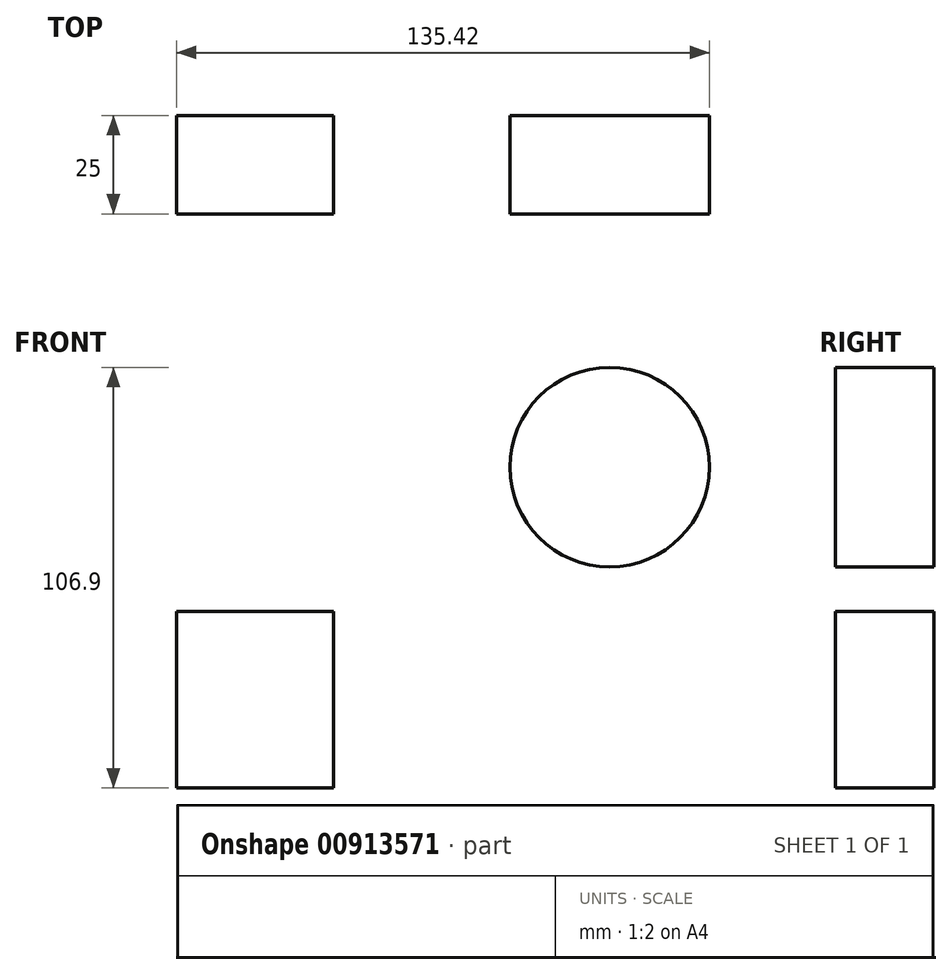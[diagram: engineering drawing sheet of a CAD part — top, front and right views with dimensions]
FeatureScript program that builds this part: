
annotation { "Feature Type Name" : "Feature", "Feature Type Description" : "" }
export const myFeature = defineFeature(function(context is Context, id is Id, definition is map)
    precondition{}
    {
        {
            var Q0;
            Q0=qCreatedBy(makeId("Front.planeOp"),FACE);
            var sketch = newSketch(context, id + "F0", { "sketchPlane" : qUnion([Q0])});
            skLineSegment(sketch, "E0.bottom", {"start": v(-147.56, 0) * mm, "end": v(-107.64, 0) * mm});
            skLineSegment(sketch, "E0.top", {"start": v(-147.56, -44.9) * mm, "end": v(-107.64, -44.9) * mm});
            skLineSegment(sketch, "E0.left", {"start": v(-147.56, 0) * mm, "end": v(-147.56, -44.9) * mm});
            skLineSegment(sketch, "E0.right", {"start": v(-107.64, 0) * mm, "end": v(-107.64, -44.9) * mm});
            skCircle(sketch, "E1", {"center": v(-37.5, 36.65) * mm, "radius": 25.35 * mm});
            skSolve(sketch);
        }
        {
            var Q0;
            Q0 = qSketchRegion(id + "F0", true);
            extrude(context, id + "F1", {"entities" : qUnion([Q0]), "depth" : 25 * mm, "offsetDistance" : 25 * mm});
        }
    });
